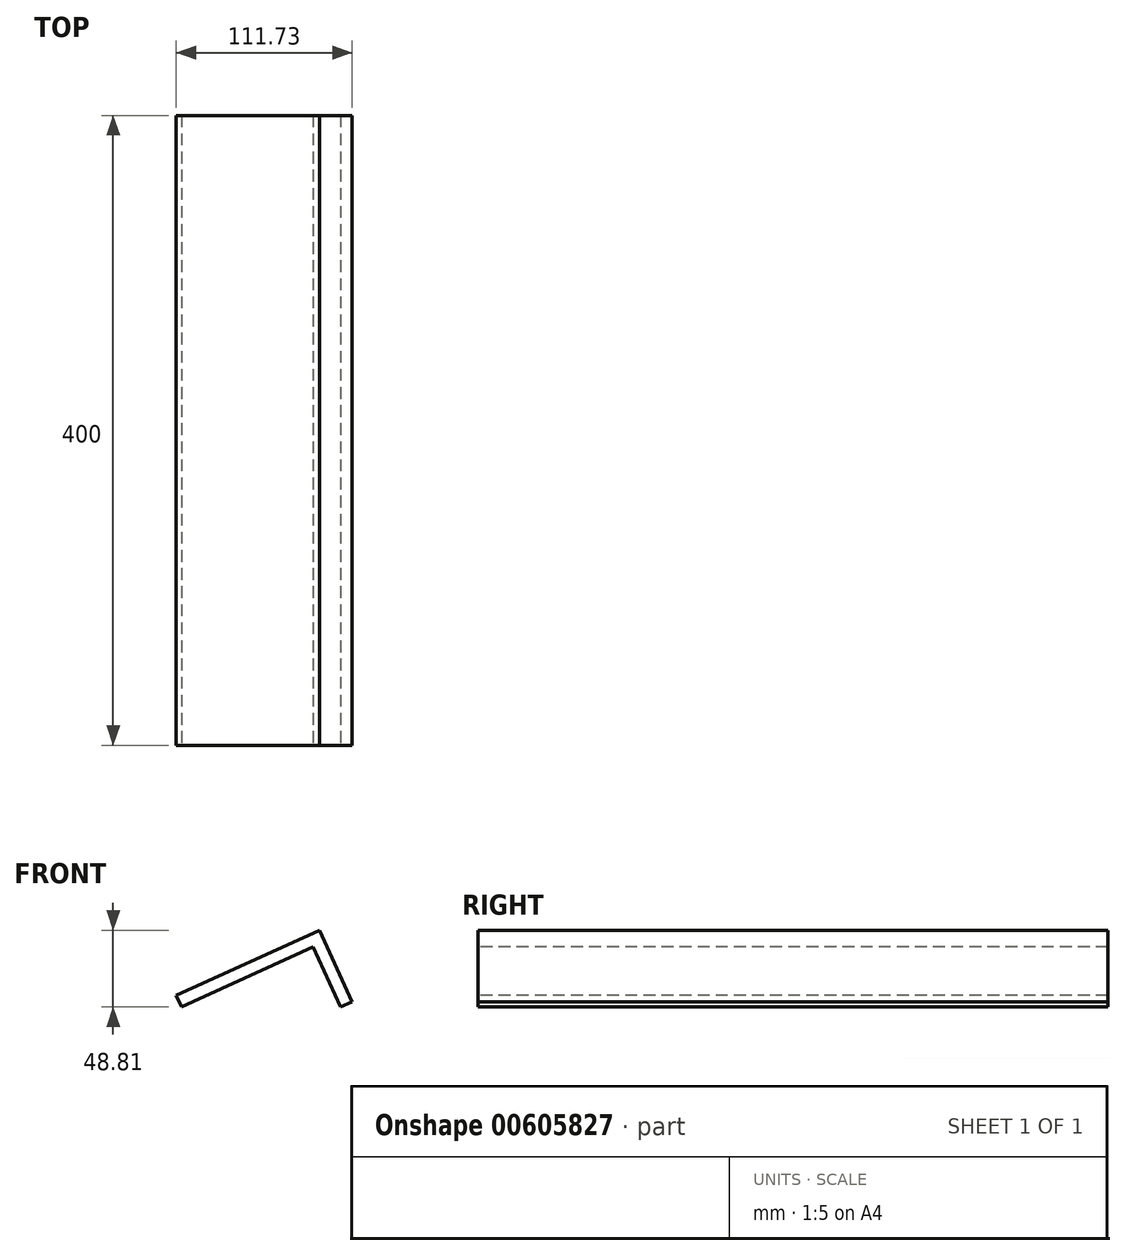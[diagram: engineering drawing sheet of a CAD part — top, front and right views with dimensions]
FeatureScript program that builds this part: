
annotation { "Feature Type Name" : "Feature", "Feature Type Description" : "" }
export const myFeature = defineFeature(function(context is Context, id is Id, definition is map)
    precondition{}
    {
        {
            var Q0;
            Q0=qCreatedBy(makeId("Front.planeOp"),FACE);
            var sketch = newSketch(context, id + "F0", { "sketchPlane" : qUnion([Q0])});
            skLineSegment(sketch, "E0", {"start": v(-87.65, 0) * mm, "end": v(-3.96, 38.2) * mm});
            skLineSegment(sketch, "E1", {"start": v(-3.96, 38.2) * mm, "end": v(13.49, 0) * mm});
            skLineSegment(sketch, "E2", {"start": v(13.49, 0) * mm, "end": v(20.76, 3.32) * mm});
            skLineSegment(sketch, "E3", {"start": v(20.76, 3.32) * mm, "end": v(0, 48.8) * mm});
            skLineSegment(sketch, "E4", {"start": v(0, 48.8) * mm, "end": v(-90.97, 7.28) * mm});
            skLineSegment(sketch, "E5", {"start": v(-90.97, 7.28) * mm, "end": v(-87.65, 0) * mm});
            skSolve(sketch);
        }
        {
            var Q0;
            Q0 = qSketchRegion(id + "F0", true);
            extrude(context, id + "F1", {"entities" : qUnion([Q0]), "oppositeDirection" : true, "depth" : 400 * mm, "offsetDistance" : 25 * mm});
        }
        {
            var Q0;
            Q0=makeQuery(id+"F1.opExtrude","SWEPT_EDGE",EDGE,{"disambiguationData":[OSD([sQuery(id+"F0.wireOp",EDGE,"E2"),sQuery(id+"F0.wireOp",EDGE,"E3")])]});
            cPoint(context, id + "F2", {"entities" : qUnion([Q0]), "parameter" : 0.5});
        }
        {
            var Q0;
            Q0=qCreatedBy(makeId("Front.planeOp"),FACE);
            var Q1;
            Q1 = qCreatedBy(id + "F2" ,VERTEX);
            cPlane(context, id + "F3", {"entities" : qUnion([Q0, Q1]), "cplaneType" : CPlaneType.PLANE_POINT, "offset" : 25 * mm, "width" : 150 * mm, "height" : 150 * mm});
        }
        {
            var Q0;
            Q0=qCreatedBy(id+"F3.planeOp",FACE);
            var sketch = newSketch(context, id + "F4", { "sketchPlane" : qUnion([Q0])});
            skFitSpline(sketch, "E6", {"points": [v(14.17, 41.85) * mm, v(5.7, 55.11) * mm, v(-4.73, 56.21) * mm, v(-19.1, 51.08) * mm], "startDerivative": vector(-21.06, 50.15) * mm, "endDerivative": vector(-20.26, -10.37) * mm});
            skSolve(sketch);
        }
        {
            var Q0;
            Q0=sQuery(id+"F4.wireOp",VERTEX,"E6.0.internal");
            var Q1;
            Q1=makeQuery(id+"F1.opExtrude","SWEPT_FACE",FACE,{"disambiguationData":[OSD([sQuery(id+"F0.wireOp",EDGE,"E3")])]});
            cPlane(context, id + "F5", {"entities" : qUnion([Q0, Q1]), "cplaneType" : CPlaneType.PLANE_POINT, "offset" : 25 * mm, "width" : 150 * mm, "height" : 150 * mm});
        }
        {
            var Q0;
            Q0=qCreatedBy(id+"F5.planeOp",FACE);
            var sketch = newSketch(context, id + "F6", { "sketchPlane" : qUnion([Q0])});
            skLineSegment(sketch, "E7", {"start": v(200, 32.18) * mm, "end": v(200, 22.03) * mm});
            skLineSegment(sketch, "E8", {"start": v(204.51, 17.5) * mm, "end": v(221.44, 17.5) * mm});
            skFitSpline(sketch, "E9", {"points": [v(204.51, 17.5) * mm, v(202.15, 17.74) * mm, v(200.39, 19.06) * mm, v(200, 22.03) * mm], "startDerivative": vector(-10.2, -0.37) * mm, "endDerivative": vector(-0.2, 9) * mm});
            skSolve(sketch);
        }
        {
            var Q0;
            Q0=makeQuery(id+"F1.opExtrude","SWEPT_FACE",FACE,{"disambiguationData":[OSD([sQuery(id+"F0.wireOp",EDGE,"E4")])]});
            var Q1;
            Q1=sQuery(id+"F4.wireOp",VERTEX,"E6.end");
            cPlane(context, id + "F7", {"entities" : qUnion([Q0, Q1]), "cplaneType" : CPlaneType.PLANE_POINT, "offset" : 25 * mm, "width" : 150 * mm, "height" : 150 * mm});
        }
        {
            var Q0;
            Q0=qCreatedBy(id+"F7.planeOp",FACE);
            var sketch = newSketch(context, id + "F8", { "sketchPlane" : qUnion([Q0])});
            skLineSegment(sketch, "E10", {"start": v(3.85, 200) * mm, "end": v(-13.38, 200) * mm});
            skLineSegment(sketch, "E11", {"start": v(-18.63, 204.34) * mm, "end": v(-18.63, 222.3) * mm});
            skFitSpline(sketch, "E12", {"points": [v(-18.63, 204.34) * mm, v(-18.24, 201.58) * mm, v(-16.67, 200.32) * mm, v(-13.38, 200) * mm], "startDerivative": vector(0.04, -9.84) * mm, "endDerivative": vector(14.86, 0.06) * mm});
            skSolve(sketch);
        }
        {
            var Q0;
            Q0=qCreatedBy(makeId("Front.planeOp"),FACE);
            var Q1;
            Q1=sQuery(id+"F6.wireOp",VERTEX,"E8.end");
            cPlane(context, id + "F9", {"entities" : qUnion([Q0, Q1]), "cplaneType" : CPlaneType.PLANE_POINT, "offset" : 25 * mm, "width" : 150 * mm, "height" : 150 * mm});
        }
        {
            var Q0;
            Q0=qCreatedBy(id+"F9.planeOp",FACE);
            var sketch = newSketch(context, id + "F10", { "sketchPlane" : qUnion([Q0])});
            skCircle(sketch, "E13", {"center": v(20.27, 28.5) * mm, "radius": 1.5 * mm});
            skSolve(sketch);
        }
        {
            var Q0;
            Q0 = qSketchRegion(id + "F10", true);
            var Q1;
            Q1 = qConstructionFilter(qBodyType(qCreatedBy(id + "F10" ,EDGE), BodyType.WIRE), ConstructionObject.NO);
            var Q2;
            Q2 = qConstructionFilter(qBodyType(qCreatedBy(id + "F6" ,EDGE), BodyType.WIRE), ConstructionObject.NO);
            var Q3;
            Q3 = qConstructionFilter(qBodyType(qCreatedBy(id + "F4" ,EDGE), BodyType.WIRE), ConstructionObject.NO);
            var Q4;
            Q4 = qConstructionFilter(qBodyType(qCreatedBy(id + "F8" ,EDGE), BodyType.WIRE), ConstructionObject.NO);
            sweep(context, id + "F11", {"bodyType" : ToolBodyType.SURFACE, "profiles" : qUnion([Q0]), "surfaceProfiles" : qUnion([Q1]), "path" : qUnion([Q2, Q3, Q4])});
        }
    });
